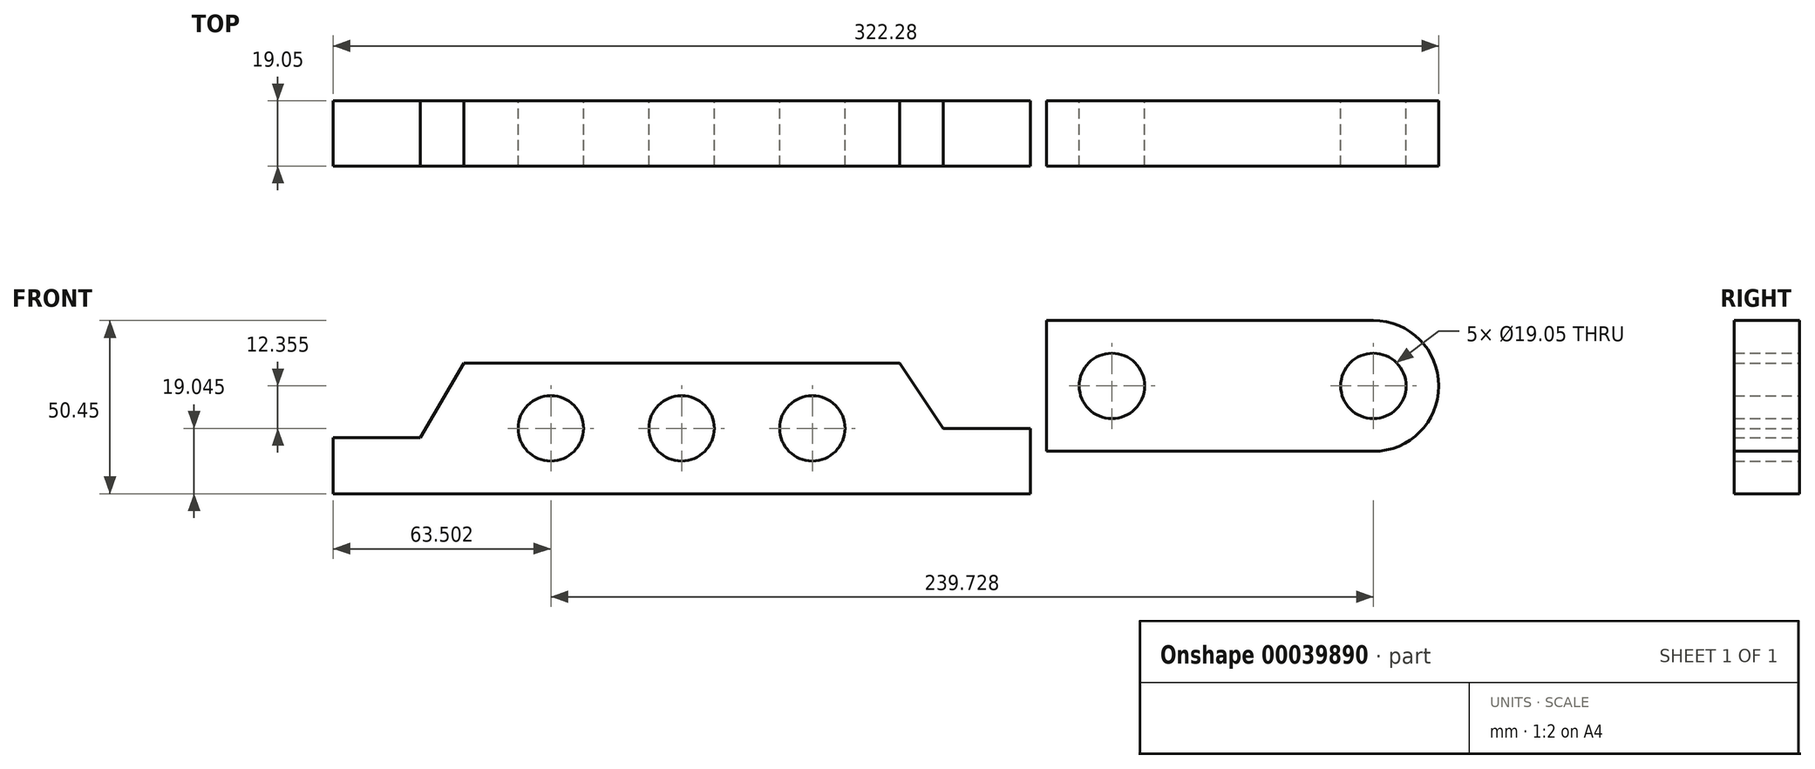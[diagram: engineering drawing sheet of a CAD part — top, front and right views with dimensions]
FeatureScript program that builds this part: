
annotation { "Feature Type Name" : "Feature", "Feature Type Description" : "" }
export const myFeature = defineFeature(function(context is Context, id is Id, definition is map)
    precondition{}
    {
        {
            var Q0;
            Q0=qCreatedBy(makeId("Front.planeOp"),FACE);
            var sketch = newSketch(context, id + "F0", { "sketchPlane" : qUnion([Q0])});
            skLineSegment(sketch, "E0.rect.bottom", {"start": v(-57.15, 19.05) * mm, "end": v(57.15, 19.05) * mm});
            skLineSegment(sketch, "E0.rect.top", {"start": v(-57.15, -19.05) * mm, "end": v(57.15, -19.05) * mm});
            skLineSegment(sketch, "E0.rect.left", {"start": v(-57.15, 19.05) * mm, "end": v(-57.15, -19.05) * mm});
            skLineSegment(sketch, "E0.rect.right", {"start": v(57.15, 19.05) * mm, "end": v(57.15, -19.05) * mm});
            skPoint(sketch, "E0.rect.middle", {"position": v(0, 0) * mm});
            skCircle(sketch, "E1", {"center": v(-38.1, 0) * mm, "radius": 9.53 * mm});
            skCircle(sketch, "E2", {"center": v(38.1, 0) * mm, "radius": 9.53 * mm});
            skSolve(sketch);
        }
        {
            var Q0;
            Q0=makeQuery(id+"F0.imprint","IMPRINT",FACE,{"disambiguationData":[TD([[makeQuery(id+"F0.imprint","IMPRINT",EDGE,{"derivedFrom":sQuery(id+"F0.wireOp",EDGE,"E0.rect.bottom")}),-1.0]])]});
            extrude(context, id + "F1", {"entities" : qUnion([Q0]), "depth" : 19.05 * mm});
        }
        {
            var Q0;
            Q0=makeQuery(id+"F1.opExtrude","SWEPT_EDGE",EDGE,{"disambiguationData":[OSD([sQuery(id+"F0.wireOp",EDGE,"E0.rect.bottom"),sQuery(id+"F0.wireOp",EDGE,"E0.rect.right")])]});
            var Q1;
            Q1=makeQuery(id+"F1.opExtrude","SWEPT_EDGE",EDGE,{"disambiguationData":[OSD([sQuery(id+"F0.wireOp",EDGE,"E0.rect.top"),sQuery(id+"F0.wireOp",EDGE,"E0.rect.right")])]});
            fillet(context, id + "F2", {"entities" : qUnion([Q0, Q1]), "radius" : 19.05 * mm, "tangentPropagation" : true, "allowEdgeOverflow" : false});
        }
        {
            var Q0;
            Q0=qCreatedBy(makeId("Front.planeOp"),FACE);
            var sketch = newSketch(context, id + "F3", { "sketchPlane" : qUnion([Q0])});
            skLineSegment(sketch, "E3", {"start": v(-227.03, 6.7) * mm, "end": v(-239.73, -15.03) * mm});
            skLineSegment(sketch, "E4", {"start": v(-239.73, -15.03) * mm, "end": v(-265.13, -15.03) * mm});
            skLineSegment(sketch, "E5", {"start": v(-265.13, -15.03) * mm, "end": v(-265.13, -31.4) * mm});
            skLineSegment(sketch, "E6", {"start": v(-265.13, -31.4) * mm, "end": v(-61.93, -31.4) * mm});
            skLineSegment(sketch, "E7", {"start": v(-227.03, 6.7) * mm, "end": v(-100.03, 6.7) * mm});
            skLineSegment(sketch, "E8", {"start": v(-61.93, -31.4) * mm, "end": v(-61.93, -12.35) * mm});
            skLineSegment(sketch, "E9", {"start": v(-61.93, -12.35) * mm, "end": v(-87.33, -12.35) * mm});
            skLineSegment(sketch, "E10", {"start": v(-100.03, 6.7) * mm, "end": v(-87.33, -12.35) * mm});
            skCircle(sketch, "E11", {"center": v(-201.63, -12.35) * mm, "radius": 9.53 * mm});
            skCircle(sketch, "E12", {"center": v(-163.53, -12.35) * mm, "radius": 9.53 * mm});
            skCircle(sketch, "E13", {"center": v(-125.43, -12.35) * mm, "radius": 9.53 * mm});
            skSolve(sketch);
        }
        {
            var Q0;
            Q0=makeQuery(id+"F3.imprint","IMPRINT",FACE,{"disambiguationData":[TD([[makeQuery(id+"F3.imprint","IMPRINT",EDGE,{"derivedFrom":sQuery(id+"F3.wireOp",EDGE,"E3")}),1.0]])]});
            extrude(context, id + "F4", {"entities" : qUnion([Q0]), "depth" : 19.05 * mm});
        }
    });
